# Revit family: Building-ConnessioniIEC309-GEWISS-44IB-PRESE-INTERBLOCCATE_IP44_SENZA_FONDO
name_source: partatom
category: Apparecchi elettrici
units: mm (PartAtom-declared; Revit-internal decimal feet)

## family parameters
Condiviso = No
Host = Superficie
Mantenere orientamento annotazione = Sì
Punto di calcolo locali = Sì
Quota connettore circolare = Usa diametro
Taglio con vuoti quando caricato = No
Tipo di parte = Normale

## types (22) — shared parameters
BLOCCO = B=C
Catalogo = BUILDING
Catalogo Serie = 44 IB
Codice Electrocod = 2220
Con fondo = No
FORMULA = 1000 mm  [stored 3.28084 ft]
Frequenza = 50/60 Hz
Frequenza nominale (Hz) = 50/60 Hz
Glow Wire Test = 850 °C (Parti attive) - 650 °C (Parti passive)
Glow wire test: = 850 °C (Parti attive) - 650 °C (Parti passive)
Grado di protezione = IP44
IDF = b5e108ce-eac4-4d9b-86d5-12d88718e221
IDT = ec1a1901-e242-435b-8cd0-c029da0151fc
Immagine tipo = IP44.jpg
L = 155 mm  [stored 0.50853 ft]
N_poli = 1
POMELLO = bianco
PRESA = Giallo
Produttore = GEWISS S.p.A.
Prospetto di default = 1219 mm
Protezione = NO (SBF)
Resistenza agli urti = IK08
SEO = Presa
STRUTTURA = RAL - 7035
STRUTTURA ALTA = blue
Scheda Tecnica = https://www.gewiss.com
Spostamento_S = 500 mm
Temperatura di funzionamento = -25 ÷ +40 °C
Temperatura di utilizzo = -25 +40 °C
Termopressione con biglia = 125 °C
Tipologia = Orizzontale
URL = https://www.gewiss.com
VETRO = Vetro
Versione file RFA = 21.4
Voltaggio = 0 V
W = 115 mm  [stored 0.377297 ft]

## per-type parameters (varying)
| type | Codice EAN | Colore | Colore: | Corrente nominale (A) | Corrente nominale (In) | Descrizione | Modello | N. poli | Numero di poli | Riferimento h | Tensione nominale |
| GW66119 - PRESA BL.OR.S.F.3P+T 32A 400V 6H SBF | 8011564029255 | Rosso | Rosso | 32 | 32 | PRESA BL.OR.S.F.3P+T 32A 400V 6H SBF | GW66119 | 3P+T | 3P+T | 6 | 380-415V |
| GW66111 - PRESA BL.OR.S.F.3P+N+T 16A 500V 7H SBF | 8011564029170 | Nero | Nero | 16 | 16 | PRESA BL.OR.S.F.3P+N+T 16A 500V 7H SBF | GW66111 | 3P+N+T | 3P+N+T | 7 | 480-500V |
| GW66108 - PRESA BL.OR.S.F.3P+T 16A 400V 6H SBF | 8011564029149 | Rosso | Rosso | 16 | 16 | PRESA BL.OR.S.F.3P+T 16A 400V 6H SBF | GW66108 | 3P+T | 3P+T | 6 | 380-415V |
| GW66117 - PRESA BL.OR.S.F.3P+N+T 32A 230V 9H SBF | 8011564029231 | Blu | Blu | 32 | 32 | PRESA BL.OR.S.F.3P+N+T 32A 230V 9H SBF | GW66117 | 3P+N+T | 3P+N+T | 9 | 200-250V |
| GW66110 - PRESA BL.OR.S.F.3P+T 16A 500V 7H SBF | 8011564029163 | Nero | Nero | 16 | 16 | PRESA BL.OR.S.F.3P+T 16A 500V 7H SBF | GW66110 | 3P+T | 3P+T | 7 | 480-500V |
| GW66104 - PRESA BL.OR.S.F.2P+T 16A 230V 6H SBF | 8011564029101 | Blu | Blu | 16 | 16 | PRESA BL.OR.S.F.2P+T 16A 230V 6H SBF | GW66104 | 2P+T | 2P+T | 6 | 200-250V |
| GW66114 - PRESA BL.OR.S.F.3P+N+T 32A 110V 4H SBF | 8011564029200 | Giallo | Giallo | 32 | 32 | PRESA BL.OR.S.F.3P+N+T 32A 110V 4H SBF | GW66114 | 3P+N+T | 3P+N+T | 4 | 100-130V |
| GW66121 - PRESA BL.OR.S.F.3P+T 32A 500V 7H SBF | 8011564029279 | Nero | Nero | 32 | 32 | PRESA BL.OR.S.F.3P+T 32A 500V 7H SBF | GW66121 | 3P+T | 3P+T | 7 | 480-500V |
| GW66113 - PRESA BL.OR.S.F.3P+T 32A 110V 4H SBF | 8011564029194 | Giallo | Giallo | 32 | 32 | PRESA BL.OR.S.F.3P+T 32A 110V 4H SBF | GW66113 | 3P+T | 3P+T | 4 | 100-130V |
| GW66120 - PRESA BL.OR.S.F.3P+N+T 32A 400V 6H SBF | 8011564029262 | Rosso | Rosso | 32 | 32 | PRESA BL.OR.S.F.3P+N+T 32A 400V 6H SBF | GW66120 | 3P+N+T | 3P+N+T | 6 | 380-415V |
| GW66112 - PRESA BL.OR.S.F.2P+T 32A 110V 4H SBF | 8011564029187 | Giallo | Giallo | 32 | 32 | PRESA BL.OR.S.F.2P+T 32A 110V 4H SBF | GW66112 | 2P+T | 2P+T | 4 | 100-130V |
| GW66115 - PRESA BL.OR.S.F.2P+T 32A 230V 6H SBF | 8011564029217 | Blu | Blu | 32 | 32 | PRESA BL.OR.S.F.2P+T 32A 230V 6H SBF | GW66115 | 2P+T | 2P+T | 6 | 200-250V |
| GW66105 - PRESA BL.OR.S.F.3P+T 16A 230V 9H SBF | 8011564029118 | Blu | Blu | 16 | 16 | PRESA BL.OR.S.F.3P+T 16A 230V 9H SBF | GW66105 | 3P+T | 3P+T | 9 | 200-250V |
| GW66102 - PRESA BL.OR.S.F.3P+T 16A 110V 4H SBF | 8011564029088 | Giallo | Giallo | 16 | 16 | PRESA BL.OR.S.F.3P+T 16A 110V 4H SBF | GW66102 | 3P+T | 3P+T | 4 | 100-130V |
| GW66107 - PRESA BL.OR.S.F.2P+T 16A 400V 9H SBF | 8011564029132 | Rosso | Rosso | 16 | 16 | PRESA BL.OR.S.F.2P+T 16A 400V 9H SBF | GW66107 | 2P+T | 2P+T | 9 | 380-415V |
| GW66116 - PRESA BL.OR.S.F.3P+T 32A 230V 9H SBF | 8011564029224 | Blu | Blu | 32 | 32 | PRESA BL.OR.S.F.3P+T 32A 230V 9H SBF | GW66116 | 3P+T | 3P+T | 9 | 200-250V |
| GW66122 - PRESA BL.OR.S.F.3P+N+T 32A 500V 7H SBF | 8011564029286 | Nero | Nero | 32 | 32 | PRESA BL.OR.S.F.3P+N+T 32A 500V 7H SBF | GW66122 | 3P+N+T | 3P+N+T | 7 | 480-500V |
| GW66109 - PRESA BL.OR.S.F.3P+N+T 16A 400V 6H SBF | 8011564029156 | Rosso | Rosso | 16 | 16 | PRESA BL.OR.S.F.3P+N+T 16A 400V 6H SBF | GW66109 | 3P+N+T | 3P+N+T | 6 | 380-415V |
| GW66106 - PRESA BL.OR.S.F.3P+N+T 16A 230V 9H SBF | 8011564029125 | Blu | Blu | 16 | 16 | PRESA BL.OR.S.F.3P+N+T 16A 230V 9H SBF | GW66106 | 3P+N+T | 3P+N+T | 9 | 200-250V |
| GW66118 - PRESA BL.OR.S.F.2P+T 32A 400V 9H SBF | 8011564029248 | Rosso | Rosso | 32 | 32 | PRESA BL.OR.S.F.2P+T 32A 400V 9H SBF | GW66118 | 2P+T | 2P+T | 9 | 380-415V |
| GW66103 - PRESA BL.OR.S.F.3P+N+T 16A 110V 4H SBF | 8011564029095 | Giallo | Giallo | 16 | 16 | PRESA BL.OR.S.F.3P+N+T 16A 110V 4H SBF | GW66103 | 3P+N+T | 3P+N+T | 4 | 100-130V |
| GW66101 - PRESA BL.OR.S.F.2P+T 16A 110V 4H SBF | 8011564029071 | Giallo | Giallo | 16 | 16 | PRESA BL.OR.S.F.2P+T 16A 110V 4H SBF | GW66101 | 2P+T | 2P+T | 4 | 100-130V |

note: [stored X ft] marks values corroborated as IEEE doubles in the binary element streams (Revit-internal decimal feet)

## geometry (parser evidence)
native form markers: Sweep x3
no freeform markers — native parametric forms only
